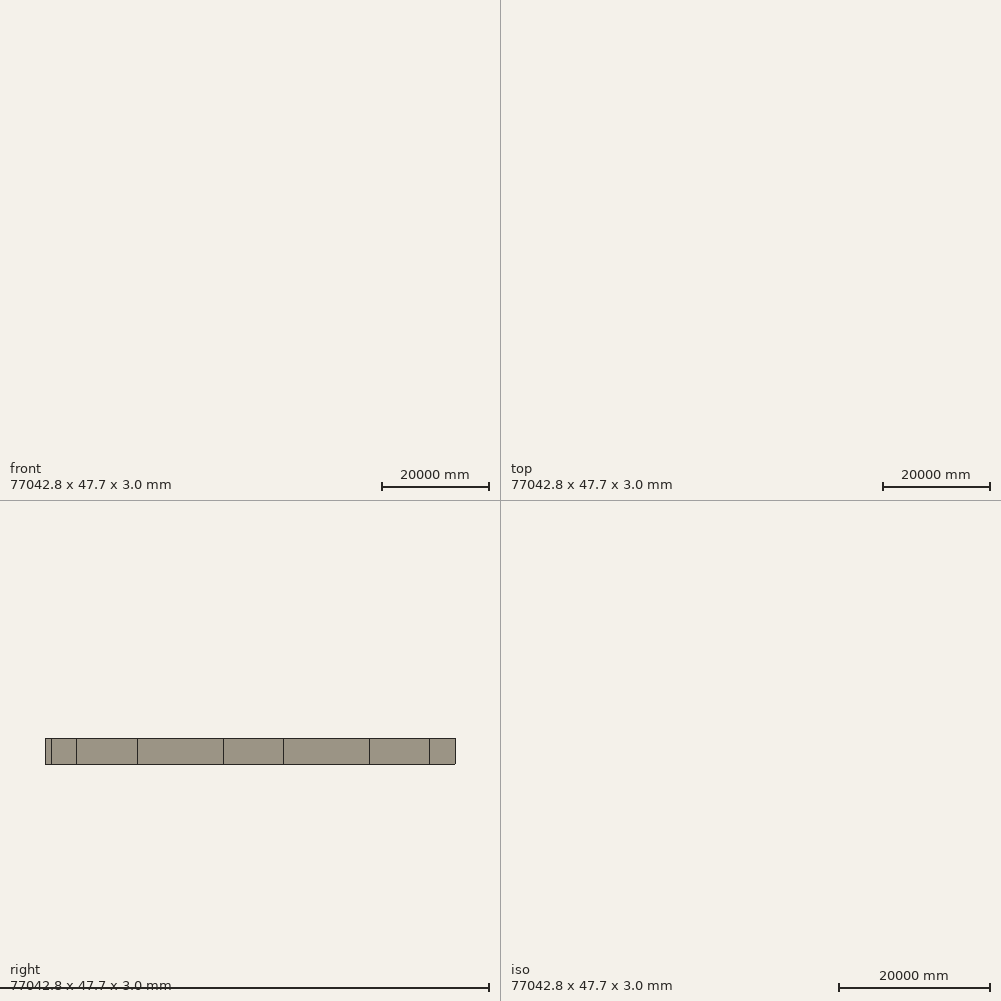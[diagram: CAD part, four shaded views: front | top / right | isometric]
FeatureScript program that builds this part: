
annotation { "Feature Type Name" : "Feature", "Feature Type Description" : "" }
export const myFeature = defineFeature(function(context is Context, id is Id, definition is map)
    precondition{}
    {
        {
            var Q0;
            Q0=qCreatedBy(makeId("Top.planeOp"),FACE);
            var sketch = newSketch(context, id + "F0", { "sketchPlane" : qUnion([Q0])});
            skLineSegment(sketch, "E0.left", {"start": v(-26, 10.25) * mm, "end": v(-26, -10.25) * mm});
            skLineSegment(sketch, "E0.right", {"start": v(26, 10.25) * mm, "end": v(26, -10.25) * mm});
            skPoint(sketch, "E0.middle", {"position": v(0, 0) * mm});
            skLineSegment(sketch, "E1", {"start": v(26, 10.25) * mm, "end": v(26, 13.25) * mm});
            skLineSegment(sketch, "E2", {"start": v(26, 13.25) * mm, "end": v(21, 13.25) * mm});
            skLineSegment(sketch, "E3", {"start": v(21, 13.25) * mm, "end": v(21, 10.25) * mm});
            skLineSegment(sketch, "E4", {"start": v(1, 10.25) * mm, "end": v(1, 13.25) * mm});
            skLineSegment(sketch, "E5", {"start": v(1, 13.25) * mm, "end": v(-9, 13.25) * mm});
            skLineSegment(sketch, "E6", {"start": v(-9, 13.25) * mm, "end": v(-9, 10.25) * mm});
            skLineSegment(sketch, "E7", {"start": v(-26, 3.25) * mm, "end": v(-29, 3.25) * mm});
            skLineSegment(sketch, "E8", {"start": v(-29, -6.75) * mm, "end": v(-26, -6.75) * mm});
            skLineSegment(sketch, "E9", {"start": v(10, -1.75) * mm, "end": v(12, -1.75) * mm});
            skLineSegment(sketch, "E10", {"start": v(10, 4.25) * mm, "end": v(9, 4.25) * mm});
            skLineSegment(sketch, "E11", {"start": v(9, 4.25) * mm, "end": v(9, 2.25) * mm});
            skLineSegment(sketch, "E12", {"start": v(13, 2.25) * mm, "end": v(13, 4.25) * mm});
            skLineSegment(sketch, "E13", {"start": v(9, 2.25) * mm, "end": v(10, 2.25) * mm});
            skLineSegment(sketch, "E14", {"start": v(13, 2.25) * mm, "end": v(12, 2.25) * mm});
            skLineSegment(sketch, "E15", {"start": v(13, 4.25) * mm, "end": v(12, 4.25) * mm});
            skLineSegment(sketch, "E16", {"start": v(12, 10.25) * mm, "end": v(21, 10.25) * mm});
            skLineSegment(sketch, "E17", {"start": v(10, 10.25) * mm, "end": v(1, 10.25) * mm});
            skLineSegment(sketch, "E18", {"start": v(-9, 10.25) * mm, "end": v(-26, 10.25) * mm});
            skLineSegment(sketch, "E19", {"start": v(10, 4.25) * mm, "end": v(10, 10.25) * mm});
            skLineSegment(sketch, "E20", {"start": v(10, 2.25) * mm, "end": v(10, -1.75) * mm});
            skLineSegment(sketch, "E21", {"start": v(12, 4.25) * mm, "end": v(12, 10.25) * mm});
            skLineSegment(sketch, "E22", {"start": v(12, 2.25) * mm, "end": v(12, -1.75) * mm});
            skLineSegment(sketch, "E23.MirrorCS", {"start": v(9, -25.25) * mm, "end": v(10, -25.25) * mm});
            skLineSegment(sketch, "E24.MirrorCS", {"start": v(12.97, -27.25) * mm, "end": v(11.97, -27.25) * mm});
            skLineSegment(sketch, "E25.MirrorCS", {"start": v(12.97, -25.25) * mm, "end": v(11.97, -25.25) * mm});
            skLineSegment(sketch, "E26.MirrorCS", {"start": v(10, -27.25) * mm, "end": v(9, -27.25) * mm});
            skLineSegment(sketch, "E27.MirrorCS", {"start": v(-26, -23.75) * mm, "end": v(-29, -23.75) * mm});
            skLineSegment(sketch, "E28.MirrorCS", {"start": v(-9, -33.75) * mm, "end": v(-9, -30.75) * mm});
            skLineSegment(sketch, "E29.MirrorCS", {"start": v(10, -30.75) * mm, "end": v(0.97, -30.75) * mm});
            skLineSegment(sketch, "E30.MirrorCS", {"start": v(10, -27.25) * mm, "end": v(10, -30.75) * mm});
            skLineSegment(sketch, "E31.MirrorCS", {"start": v(10, -25.25) * mm, "end": v(10, -18.75) * mm});
            skLineSegment(sketch, "E32.MirrorCS", {"start": v(0.97, -30.75) * mm, "end": v(0.98, -33.75) * mm});
            skLineSegment(sketch, "E33.MirrorCS", {"start": v(11.97, -25.25) * mm, "end": v(11.97, -18.75) * mm});
            skLineSegment(sketch, "E34.MirrorCS", {"start": v(11.97, -27.25) * mm, "end": v(11.97, -30.75) * mm});
            skLineSegment(sketch, "E35.MirrorCS", {"start": v(10, -18.75) * mm, "end": v(11.97, -18.75) * mm});
            skLineSegment(sketch, "E36.MirrorCS", {"start": v(0.98, -33.75) * mm, "end": v(-9, -33.75) * mm});
            skLineSegment(sketch, "E37.MirrorCS", {"start": v(-29, -13.75) * mm, "end": v(-26, -13.75) * mm});
            skLineSegment(sketch, "E38.MirrorCS", {"start": v(11.97, -30.75) * mm, "end": v(20.97, -30.75) * mm});
            skLineSegment(sketch, "E39.MirrorCS", {"start": v(21, -34.4) * mm, "end": v(20.97, -30.75) * mm});
            skLineSegment(sketch, "E40.MirrorCS", {"start": v(12.97, -25.25) * mm, "end": v(12.97, -27.25) * mm});
            skLineSegment(sketch, "E41.MirrorCS", {"start": v(26, -30.75) * mm, "end": v(26, -33.75) * mm});
            skLineSegment(sketch, "E42.MirrorCS", {"start": v(9, -27.25) * mm, "end": v(9, -25.25) * mm});
            skLineSegment(sketch, "E43.MirrorCS", {"start": v(-26, -30.75) * mm, "end": v(-26, -10.25) * mm});
            skLineSegment(sketch, "E44.MirrorCS", {"start": v(-9, -30.75) * mm, "end": v(-26, -30.75) * mm});
            skPoint(sketch, "E45.MirrorP", {"position": v(0, -20.5) * mm});
            skLineSegment(sketch, "E46.MirrorCS", {"start": v(26, -30.75) * mm, "end": v(26, -10.25) * mm});
            skLineSegment(sketch, "E47.MirrorCS", {"start": v(39, 4.25) * mm, "end": v(40, 4.25) * mm});
            skLineSegment(sketch, "E48.MirrorCS", {"start": v(43, -27.25) * mm, "end": v(43, -25.25) * mm});
            skLineSegment(sketch, "E49.MirrorCS", {"start": v(39, 2.25) * mm, "end": v(40, 2.25) * mm});
            skLineSegment(sketch, "E50.MirrorCS", {"start": v(42, -27.25) * mm, "end": v(43, -27.25) * mm});
            skLineSegment(sketch, "E51.MirrorCS", {"start": v(39, 2.25) * mm, "end": v(39, 4.25) * mm});
            skLineSegment(sketch, "E52.MirrorCS", {"start": v(39.03, -25.25) * mm, "end": v(39.03, -27.25) * mm});
            skLineSegment(sketch, "E53.MirrorCS", {"start": v(43, -25.25) * mm, "end": v(42, -25.25) * mm});
            skLineSegment(sketch, "E54.MirrorCS", {"start": v(43, 4.25) * mm, "end": v(43, 2.25) * mm});
            skLineSegment(sketch, "E55.MirrorCS", {"start": v(43, 2.25) * mm, "end": v(42, 2.25) * mm});
            skLineSegment(sketch, "E56.MirrorCS", {"start": v(42, 4.25) * mm, "end": v(43, 4.25) * mm});
            skLineSegment(sketch, "E57.MirrorCS", {"start": v(39.03, -27.25) * mm, "end": v(40.03, -27.25) * mm});
            skLineSegment(sketch, "E58.MirrorCS", {"start": v(42, -18.75) * mm, "end": v(40.03, -18.75) * mm});
            skLineSegment(sketch, "E59.MirrorCS", {"start": v(61, -33.75) * mm, "end": v(61, -30.75) * mm});
            skLineSegment(sketch, "E60.MirrorCS", {"start": v(42, 4.25) * mm, "end": v(42, 10.25) * mm});
            skLineSegment(sketch, "E61.MirrorCS", {"start": v(42, -27.25) * mm, "end": v(42, -30.75) * mm});
            skLineSegment(sketch, "E62.MirrorCS", {"start": v(40.03, -27.25) * mm, "end": v(40.03, -30.75) * mm});
            skLineSegment(sketch, "E63.MirrorCS", {"start": v(40, 4.25) * mm, "end": v(40, 10.25) * mm});
            skLineSegment(sketch, "E64.MirrorCS", {"start": v(39.03, -25.25) * mm, "end": v(40.03, -25.25) * mm});
            skLineSegment(sketch, "E65.MirrorCS", {"start": v(31, -34.4) * mm, "end": v(31.03, -30.75) * mm});
            skLineSegment(sketch, "E66.MirrorCS", {"start": v(31, 13.25) * mm, "end": v(31, 10.25) * mm});
            skLineSegment(sketch, "E67.MirrorCS", {"start": v(51, 10.25) * mm, "end": v(51, 13.25) * mm});
            skLineSegment(sketch, "E68.MirrorCS", {"start": v(51.03, -30.75) * mm, "end": v(51.02, -33.75) * mm});
            skLineSegment(sketch, "E69.MirrorCS", {"start": v(61, 13.25) * mm, "end": v(61, 10.25) * mm});
            skLineSegment(sketch, "E70.MirrorCS", {"start": v(42, -1.75) * mm, "end": v(40, -1.75) * mm});
            skLineSegment(sketch, "E71.MirrorCS", {"start": v(78, -23.75) * mm, "end": v(81, -23.75) * mm});
            skLineSegment(sketch, "E72.MirrorCS", {"start": v(81, -13.75) * mm, "end": v(78, -13.75) * mm});
            skLineSegment(sketch, "E73.MirrorCS", {"start": v(78, 3.25) * mm, "end": v(81, 3.25) * mm});
            skLineSegment(sketch, "E74.MirrorCS", {"start": v(81, -6.75) * mm, "end": v(78, -6.75) * mm});
            skLineSegment(sketch, "E75.MirrorCS", {"start": v(42, -25.25) * mm, "end": v(42, -18.75) * mm});
            skLineSegment(sketch, "E76.MirrorCS", {"start": v(40, 2.25) * mm, "end": v(40, -1.75) * mm});
            skPoint(sketch, "E77.MirrorP", {"position": v(52, 0) * mm});
            skLineSegment(sketch, "E78.MirrorCS", {"start": v(61, -30.75) * mm, "end": v(78, -30.75) * mm});
            skLineSegment(sketch, "E79.MirrorCS", {"start": v(61, 10.25) * mm, "end": v(78, 10.25) * mm});
            skLineSegment(sketch, "E80.MirrorCS", {"start": v(42, -30.75) * mm, "end": v(51.03, -30.75) * mm});
            skLineSegment(sketch, "E81.MirrorCS", {"start": v(78, -30.75) * mm, "end": v(78, -10.25) * mm});
            skPoint(sketch, "E82.MirrorP", {"position": v(52, -20.5) * mm});
            skLineSegment(sketch, "E83.MirrorCS", {"start": v(26, 13.25) * mm, "end": v(31, 13.25) * mm});
            skLineSegment(sketch, "E84.MirrorCS", {"start": v(51, 13.25) * mm, "end": v(61, 13.25) * mm});
            skLineSegment(sketch, "E85.MirrorCS", {"start": v(40.03, -30.75) * mm, "end": v(31.03, -30.75) * mm});
            skLineSegment(sketch, "E86.MirrorCS", {"start": v(40, 10.25) * mm, "end": v(31, 10.25) * mm});
            skLineSegment(sketch, "E87.MirrorCS", {"start": v(78, 10.25) * mm, "end": v(78, -10.25) * mm});
            skLineSegment(sketch, "E88.MirrorCS", {"start": v(40.03, -25.25) * mm, "end": v(40.03, -18.75) * mm});
            skLineSegment(sketch, "E89.MirrorCS", {"start": v(42, 10.25) * mm, "end": v(51, 10.25) * mm});
            skLineSegment(sketch, "E90.MirrorCS", {"start": v(42, 2.25) * mm, "end": v(42, -1.75) * mm});
            skLineSegment(sketch, "E91.MirrorCS", {"start": v(51.02, -33.75) * mm, "end": v(61, -33.75) * mm});
            skLineSegment(sketch, "E92", {"start": v(-29, -6.75) * mm, "end": v(-29, -13.75) * mm});
            skLineSegment(sketch, "E93", {"start": v(-29, 3.25) * mm, "end": v(-29, 10.25) * mm});
            skLineSegment(sketch, "E94", {"start": v(-29, 10.25) * mm, "end": v(-26, 10.25) * mm});
            skLineSegment(sketch, "E95.MirrorCS", {"start": v(-29, -13.75) * mm, "end": v(-29, -6.75) * mm});
            skLineSegment(sketch, "E96.MirrorCS", {"start": v(-29, -23.75) * mm, "end": v(-29, -30.75) * mm});
            skLineSegment(sketch, "E97.MirrorCS", {"start": v(76990.58, -30.75) * mm, "end": v(76990.58, -10.25) * mm});
            skLineSegment(sketch, "E98.MirrorCS", {"start": v(76990.58, -30.75) * mm, "end": v(-9, -30.75) * mm});
            skLineSegment(sketch, "E99.MirrorCS", {"start": v(-29, -30.75) * mm, "end": v(76990.58, -30.75) * mm});
            skLineSegment(sketch, "E100.MirrorCS", {"start": v(81, -30.75) * mm, "end": v(-76938.58, -30.75) * mm});
            skLineSegment(sketch, "E101.MirrorCS", {"start": v(81, 10.25) * mm, "end": v(78, 10.25) * mm});
            skLineSegment(sketch, "E102.MirrorCS", {"start": v(-76938.58, -30.75) * mm, "end": v(61, -30.75) * mm});
            skLineSegment(sketch, "E103.MirrorCS", {"start": v(81, -13.75) * mm, "end": v(81, -6.75) * mm});
            skLineSegment(sketch, "E104.MirrorCS", {"start": v(81, 3.25) * mm, "end": v(81, 10.25) * mm});
            skLineSegment(sketch, "E105.MirrorCS", {"start": v(-76938.58, -30.75) * mm, "end": v(-76938.58, -10.25) * mm});
            skLineSegment(sketch, "E106.MirrorCS", {"start": v(81, -6.75) * mm, "end": v(81, -13.75) * mm});
            skLineSegment(sketch, "E107.MirrorCS", {"start": v(81, -23.75) * mm, "end": v(81, -30.75) * mm});
            skPoint(sketch, "E108.MirrorCS.end.orphan", {"position": v(-32, -13.7) * mm});
            skPoint(sketch, "E109.MirrorCS.end.orphan", {"position": v(-32, -23.75) * mm});
            skPoint(sketch, "E110.end.orphan", {"position": v(-32, -6.8) * mm});
            skPoint(sketch, "E111.end.orphan", {"position": v(-32, 3.25) * mm});
            skPoint(sketch, "E112.MirrorCS.start.orphan", {"position": v(84, -13.7) * mm});
            skPoint(sketch, "E113.MirrorCS.end.orphan", {"position": v(84, -23.75) * mm});
            skPoint(sketch, "E114.MirrorCS.end.orphan", {"position": v(84, 3.25) * mm});
            skPoint(sketch, "E115.MirrorCS.start.orphan", {"position": v(84, -6.8) * mm});
            skCircle(sketch, "E116", {"center": v(-76958.58, -10) * mm, "radius": 3.25 * mm});
            skLineSegment(sketch, "E117", {"start": v(21, -34.4) * mm, "end": v(31, -34.4) * mm});
            skSolve(sketch);
        }
        {
            var Q0;
            Q0 = qSketchRegion(id + "F0", true);
            extrude(context, id + "F1", {"entities" : qUnion([Q0]), "endBound" : BoundingType.SYMMETRIC, "depth" : 3 * mm});
        }
    });
